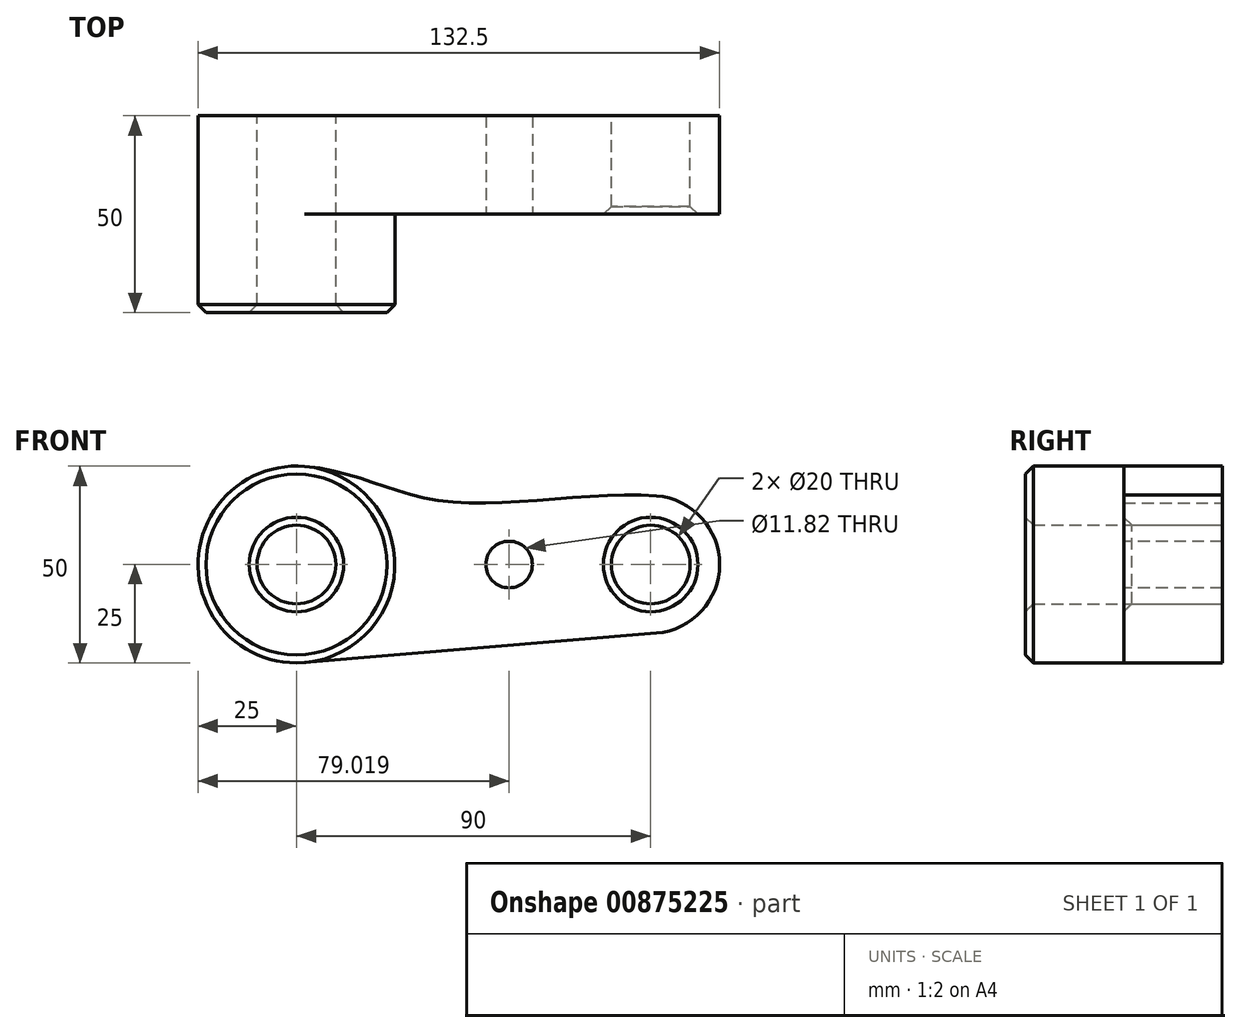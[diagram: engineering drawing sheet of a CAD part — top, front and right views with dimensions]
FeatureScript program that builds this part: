
annotation { "Feature Type Name" : "Feature", "Feature Type Description" : "" }
export const myFeature = defineFeature(function(context is Context, id is Id, definition is map)
    precondition{}
    {
        {
            var Q0;
            Q0=qCreatedBy(makeId("Front.planeOp"),FACE);
            var sketch = newSketch(context, id + "F0", { "sketchPlane" : qUnion([Q0])});
            skCircle(sketch, "E0", {"center": v(0, 0) * mm, "radius": 25 * mm});
            skCircle(sketch, "E1", {"center": v(90, 0) * mm, "radius": 17.5 * mm});
            skLineSegment(sketch, "E2", {"start": v(2.08, 24.91) * mm, "end": v(91.46, 17.44) * mm});
            skLineSegment(sketch, "E3", {"start": v(2.08, -24.91) * mm, "end": v(91.46, -17.44) * mm});
            skCircle(sketch, "E4", {"center": v(0, 0) * mm, "radius": 10 * mm});
            skCircle(sketch, "E5", {"center": v(90, 0) * mm, "radius": 10 * mm});
            skFitSpline(sketch, "E6", {"points": [v(91.46, 17.44) * mm, v(37.37, 16.1) * mm, v(2.08, 24.91) * mm], "startDerivative": vector(-89.38, 7.47) * mm, "endDerivative": vector(-89.38, 7.47) * mm});
            skSolve(sketch);
        }
        {
            var Q0;
            {var subQ3=sQuery(id+"F0.wireOp",EDGE,"E3");Q0=makeQuery(id+"F0.imprint","IMPRINT",FACE,{"disambiguationData":[TD([[makeQuery(id+"F0.imprint","IMPRINT",EDGE,{"derivedFrom":subQ3}),1.0]])]});}
            var Q1;
            Q1=makeQuery(id+"F0.imprint","IMPRINT",FACE,{"disambiguationData":[TD([[makeQuery(id+"F0.imprint","IMPRINT",EDGE,{"derivedFrom":sQuery(id+"F0.wireOp",EDGE,"E4")}),-1.0]])]});
            var Q2;
            Q2=makeQuery(id+"F0.imprint","IMPRINT",FACE,{"disambiguationData":[TD([[makeQuery(id+"F0.imprint","IMPRINT",EDGE,{"derivedFrom":sQuery(id+"F0.wireOp",EDGE,"E5")}),-1.0]])]});
            extrude(context, id + "F1", {"entities" : qUnion([Q0, Q1, Q2]), "offsetDistance" : 25 * mm, "depth" : 25 * mm});
        }
        {
            var Q0;
            Q0=makeQuery(id+"F0.imprint","IMPRINT",FACE,{"disambiguationData":[TD([[makeQuery(id+"F0.imprint","IMPRINT",EDGE,{"derivedFrom":sQuery(id+"F0.wireOp",EDGE,"E4")}),-1.0]])]});
            extrude(context, id + "F2", {"entities" : qUnion([Q0]), "operationType" : NewBodyOperationType.ADD, "depth" : 50 * mm});
        }
        {
            var Q0;
            Q0=makeQuery(id+"F2.opExtrude","CAP_EDGE",EDGE,{"disambiguationData":[OSD([sQuery(id+"F0.wireOp",EDGE,"E0")])],"isStart":false});
            var Q1;
            Q1=makeQuery(id+"F2.opExtrude","CAP_EDGE",EDGE,{"disambiguationData":[OSD([sQuery(id+"F0.wireOp",EDGE,"E4")])],"isStart":false});
            var Q2;
            Q2=makeQuery(id+"F1.opExtrude","CAP_EDGE",EDGE,{"disambiguationData":[OSD([sQuery(id+"F0.wireOp",EDGE,"E5")])],"isStart":false});
            chamfer(context, id + "F3", {"entities" : qUnion([Q0, Q1, Q2]), "width" : 2 * mm, "tangentPropagation" : true});
        }
        {
            var Q0;
            Q0=makeQuery(id+"F1.opExtrude","CAP_FACE",FACE,{"disambiguationData":[OSD([sQuery(id+"F0.wireOp",EDGE,"E0"),sQuery(id+"F0.wireOp",EDGE,"E1"),sQuery(id+"F0.wireOp",EDGE,"E3"),sQuery(id+"F0.wireOp",EDGE,"E4"),sQuery(id+"F0.wireOp",EDGE,"E5"),sQuery(id+"F0.wireOp",EDGE,"E6")])],"isStart":false});
            var sketch = newSketch(context, id + "F4", { "sketchPlane" : qUnion([Q0])});
            skCircle(sketch, "E7", {"center": v(54.02, 0) * mm, "radius": 5.91 * mm});
            skSolve(sketch);
        }
        {
            var Q0;
            Q0=makeQuery(id+"F4.imprint","IMPRINT",FACE,{"disambiguationData":[TD([[makeQuery(id+"F4.imprint","IMPRINT",EDGE,{"derivedFrom":sQuery(id+"F4.wireOp",EDGE,"E7")}),1.0]])]});
            extrude(context, id + "F5", {"entities" : qUnion([Q0]), "operationType" : NewBodyOperationType.REMOVE, "oppositeDirection" : true, "depth" : 25 * mm, "offsetDistance" : 25 * mm});
        }
    });
